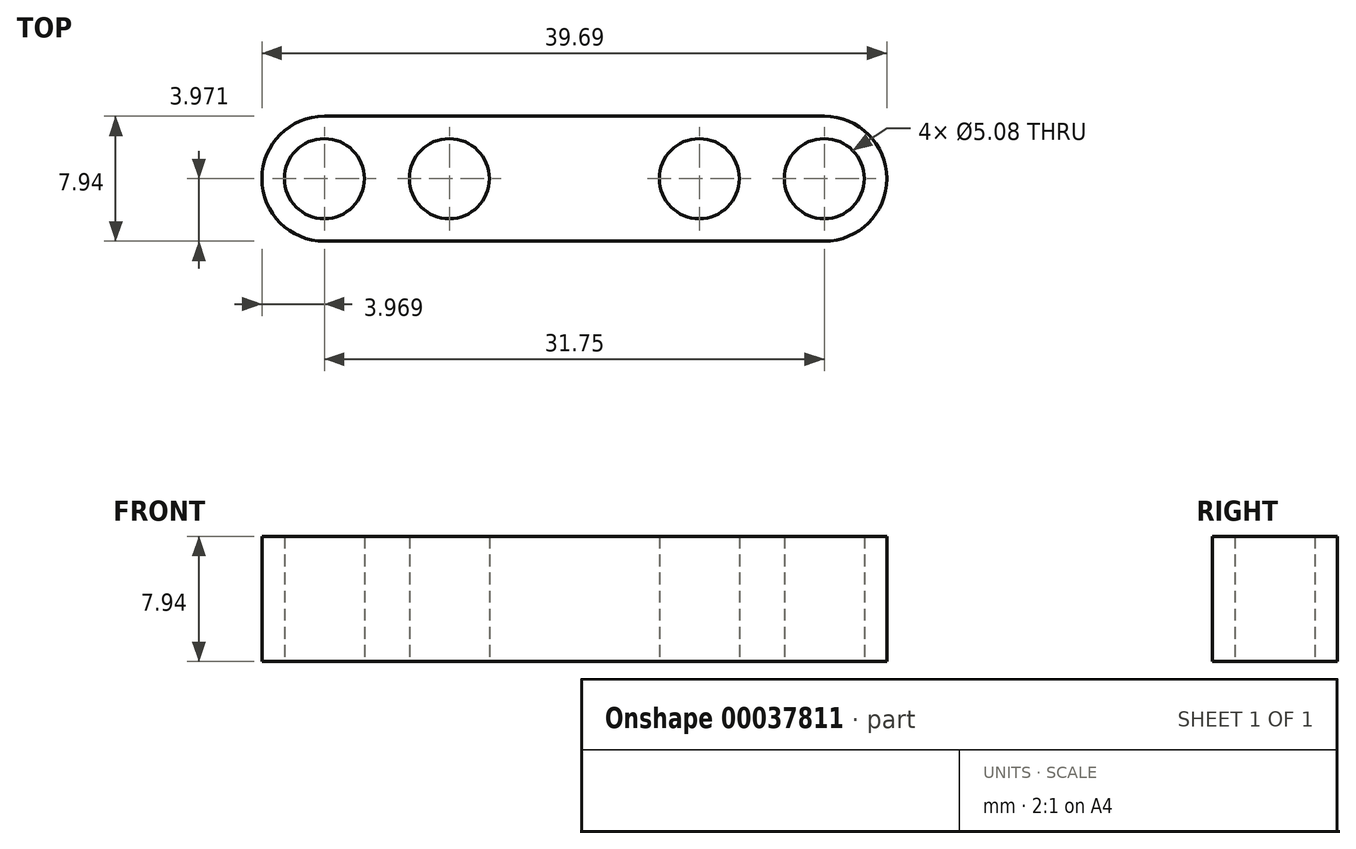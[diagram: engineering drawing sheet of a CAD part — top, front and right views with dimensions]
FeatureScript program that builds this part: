
annotation { "Feature Type Name" : "Feature", "Feature Type Description" : "" }
export const myFeature = defineFeature(function(context is Context, id is Id, definition is map)
    precondition{}
    {
        {
            var Q0;
            Q0=qCreatedBy(makeId("Top.planeOp"),FACE);
            var sketch = newSketch(context, id + "F0", { "sketchPlane" : qUnion([Q0])});
            skLineSegment(sketch, "E0.bottom", {"start": v(0, 0) * mm, "end": v(39.69, 0) * mm});
            skLineSegment(sketch, "E0.top", {"start": v(0, -7.94) * mm, "end": v(39.69, -7.94) * mm});
            skLineSegment(sketch, "E0.left", {"start": v(0, 0) * mm, "end": v(0, -7.94) * mm});
            skLineSegment(sketch, "E0.right", {"start": v(39.69, 0) * mm, "end": v(39.69, -7.94) * mm});
            skLineSegment(sketch, "E1", {"start": v(0, -3.97) * mm, "end": v(3.97, -3.97) * mm, "construction": true});
            skLineSegment(sketch, "E2", {"start": v(11.9, -3.97) * mm, "end": v(27.78, -3.97) * mm, "construction": true});
            skLineSegment(sketch, "E3", {"start": v(35.72, -3.97) * mm, "end": v(39.69, -3.97) * mm, "construction": true});
            skCircle(sketch, "E4", {"center": v(3.97, -3.97) * mm, "radius": 2.54 * mm});
            skCircle(sketch, "E5", {"center": v(11.9, -3.97) * mm, "radius": 2.54 * mm});
            skCircle(sketch, "E6", {"center": v(27.78, -3.97) * mm, "radius": 2.54 * mm});
            skCircle(sketch, "E7", {"center": v(35.72, -3.97) * mm, "radius": 2.54 * mm});
            skLineSegment(sketch, "E8", {"start": v(19.84, -3.97) * mm, "end": v(19.84, -7.94) * mm, "construction": true});
            skSolve(sketch);
        }
        {
            var Q0;
            Q0=qSketchRegion(id+"F0",true);
            extrude(context, id + "F1", {"entities" : qUnion([Q0]), "depth" : 7.94 * mm});
        }
        {
            var Q0;
            Q0=makeQuery(id+"F1.opExtrude","SWEPT_EDGE",EDGE,{"disambiguationData":[OSD([sQuery(id+"F0.wireOp",EDGE,"E0.bottom"),sQuery(id+"F0.wireOp",EDGE,"E0.left")])]});
            var Q1;
            Q1=makeQuery(id+"F1.opExtrude","SWEPT_EDGE",EDGE,{"disambiguationData":[OSD([sQuery(id+"F0.wireOp",EDGE,"E0.top"),sQuery(id+"F0.wireOp",EDGE,"E0.left")])]});
            var Q2;
            Q2=makeQuery(id+"F1.opExtrude","SWEPT_EDGE",EDGE,{"disambiguationData":[OSD([sQuery(id+"F0.wireOp",EDGE,"E0.top"),sQuery(id+"F0.wireOp",EDGE,"E0.right")])]});
            var Q3;
            Q3=makeQuery(id+"F1.opExtrude","SWEPT_EDGE",EDGE,{"disambiguationData":[OSD([sQuery(id+"F0.wireOp",EDGE,"E0.bottom"),sQuery(id+"F0.wireOp",EDGE,"E0.right")])]});
            fillet(context, id + "F2", {"entities" : qUnion([Q0, Q1, Q2, Q3]), "radius" : 3.97 * mm, "tangentPropagation" : true, "allowEdgeOverflow" : false});
        }
    });
